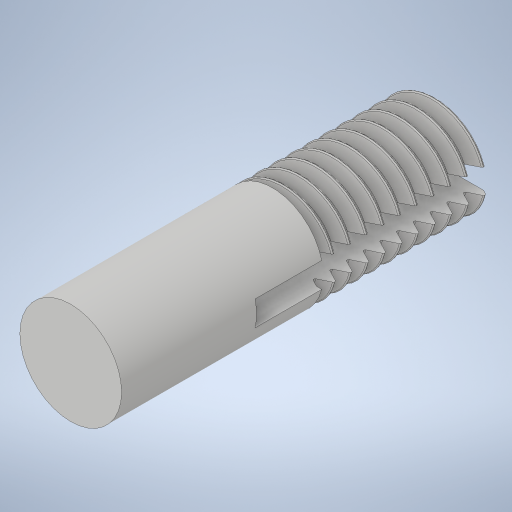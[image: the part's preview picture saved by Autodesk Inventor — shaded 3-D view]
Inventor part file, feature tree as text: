
AUTODESK INVENTOR PART (.ipt)
format: ipt  version: 2023 (Build 270158000, 158)  size: 925,696 bytes
history: native  units: mm
features: sketch x5, extrude x2, revolve x2, thread x1, helix x1, boolean_combine x1
ambient origin geometry x8: Origin, YZ Plane, XZ Plane, XY Plane, X Axis, Y Axis, Z Axis, Center Point
bodies: Solid1 (feature_tree), Solid2 (feature_tree)
feature tree (12):
  extrude  "Extrusion1"  Depth=22.1mm TaperAngle=0.0deg
  thread  "Thread1"  [1 undecoded]
  revolve  "Revolution1"  [1 undecoded]
  revolve  "Revolution2"  [1 undecoded]
  helix  "Coil1"  [1 undecoded]
  sketch  "Sketch5"  dims[d25=14.0mm d26=0.0mm d27=8.0mm d28=0.5mm d29=0.872665mm d30=0.5mm d31=0.872665mm]
  boolean_combine  "Combine1"
  extrude  "Extrusion2"  Depth=1.5mm
  sketch  "Sketch1"  dims[d0=6.1mm d1=22.1mm d2=0.0mm d3=10.0mm d4=0.0mm]
  sketch  "Sketch2"  dims[d5=9.599311mm d6=0.160083mm d7=0.160083mm d10=1.0mm]
  sketch  "Sketch3"  dims[d12=9.599311mm d14=0.0mm d15=0.0mm]
  sketch  "Sketch4"  dims[d16=1.001mm d17=12.0mm d18=10.0mm d19=0.0mm d20=0.0mm d21=0.0mm d22=0.0mm d23=0.0mm d24=1.5mm]
note: 4 required parameter values undecoded (feature->parameter linkage not recoverable at this tier; creation-order binding heuristic only, values carry confidence <= 0.55)